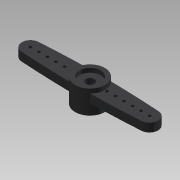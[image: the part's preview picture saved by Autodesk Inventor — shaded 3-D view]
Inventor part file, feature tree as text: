
AUTODESK INVENTOR PART (.ipt)
format: ipt  version: 2016 (Build 200138000, 138)  size: 182,272 bytes
history: native  units: mm
features: extrude x6, sketch x6, projected_geometry x4
ambient origin geometry x8: Origin, YZ Plane, XZ Plane, XY Plane, X Axis, Y Axis, Z Axis, Center Point
bodies: Solid1 (feature_tree)
feature tree (16):
  extrude  "Extrusion1"  Depth=7.0mm
  extrude  "Extrusion2"  Depth=2.0mm TaperAngle=0.0deg
  extrude  "Extrusion3"  Depth=2.0mm
  extrude  "Extrusion4"  Depth=2.0mm
  extrude  "Extrusion5"  Depth=10.0mm
  extrude  "Extrusion6"  Depth=10.0mm
  sketch  "Sketch1"  dims[d0=5.0mm d1=7.0mm]
  sketch  "Sketch2"  dims[d2=2.5mm d3=0.0mm d8=2.0mm d9=0.0mm]
  sketch  "Sketch3"  dims[d10=2.0mm d11=0.0mm d12=5.0mm]
  projected_geometry  "Projected Loop1"
  projected_geometry  "Projected Loop2"
  projected_geometry  "Projected Loop3"
  sketch  "Sketch4"  dims[d13=1.0mm d14=0.0mm d15=2.0mm]
  sketch  "Sketch5"  dims[d16=10.0mm d17=0.0mm d18=0.7mm]
  sketch  "Sketch6"  dims[d19=2.0mm d25=0.7mm d26=0.7mm d27=0.7mm d28=0.7mm d29=10.0mm d30=0.0mm]
  projected_geometry  "Projected Loop4"
